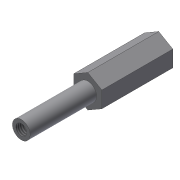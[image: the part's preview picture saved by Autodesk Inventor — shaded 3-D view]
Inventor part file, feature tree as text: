
AUTODESK INVENTOR PART (.ipt)
format: ipt  version: 2018 (Build 220112000, 112)  size: 90,624 bytes
history: native  units: mm
features: sketch x3, extrude x2, hole x1
ambient origin geometry x8: Origin, YZ Plane, XZ Plane, XY Plane, X Axis, Y Axis, Z Axis, Center Point
bodies: Solid1 (feature_tree)
feature tree (6):
  extrude  "Extrusion1"  Depth=32.0mm TaperAngle=0.0deg
  extrude  "Extrusion2"  Depth=30.0mm TaperAngle=0.0deg
  hole  "Hole1"  [1 undecoded]
  sketch  "Sketch1"  dims[d0=12.7mm d1=32.0mm d2=0.0mm]
  sketch  "Sketch2"  dims[d3=8.0mm d4=30.0mm d5=0.0mm]
  sketch  "Sketch3"  dims[d6=4.917mm d7=12.0mm d8=4.0mm d9=2.0mm d10=90.0deg d11=17.1mm d12=20.594885mm]
note: 1 required parameter value undecoded (feature->parameter linkage not recoverable at this tier; creation-order binding heuristic only, values carry confidence <= 0.55)
